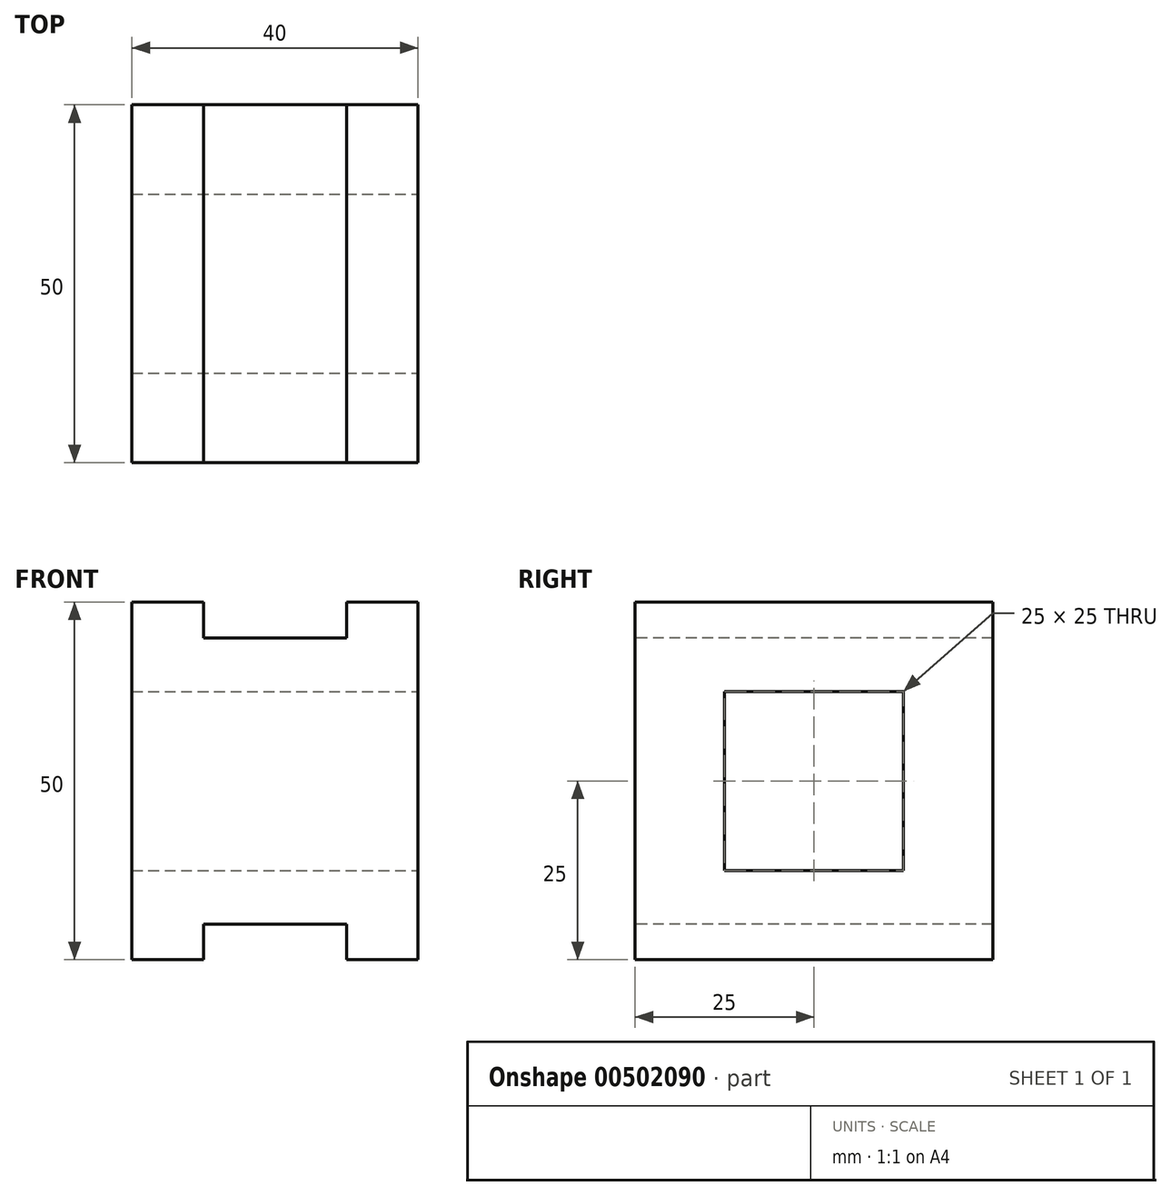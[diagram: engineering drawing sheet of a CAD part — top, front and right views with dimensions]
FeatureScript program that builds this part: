
annotation { "Feature Type Name" : "Feature", "Feature Type Description" : "" }
export const myFeature = defineFeature(function(context is Context, id is Id, definition is map)
    precondition{}
    {
        {
            var Q0;
            Q0=qCreatedBy(makeId("Front.planeOp"),FACE);
            var sketch = newSketch(context, id + "F0", { "sketchPlane" : qUnion([Q0])});
            skLineSegment(sketch, "E0.bottom", {"start": v(0, 0) * mm, "end": v(40, 0) * mm});
            skLineSegment(sketch, "E0.top", {"start": v(0, 50) * mm, "end": v(40, 50) * mm});
            skLineSegment(sketch, "E0.left", {"start": v(0, 0) * mm, "end": v(0, 50) * mm});
            skLineSegment(sketch, "E0.right", {"start": v(40, 0) * mm, "end": v(40, 50) * mm});
            skSolve(sketch);
        }
        {
            var Q0;
            Q0=makeQuery(id+"F0.imprint","IMPRINT",FACE,{"disambiguationData":[TD([[makeQuery(id+"F0.imprint","IMPRINT",EDGE,{"derivedFrom":sQuery(id+"F0.wireOp",EDGE,"E0.bottom")}),1.0]])]});
            extrude(context, id + "F1", {"entities" : qUnion([Q0]), "oppositeDirection" : true, "depth" : 50 * mm, "offsetDistance" : 25 * mm});
        }
        {
            var Q0;
            Q0=makeQuery(id+"F1.opExtrude","SWEPT_FACE",FACE,{"disambiguationData":[OSD([sQuery(id+"F0.wireOp",EDGE,"E0.right")])]});
            var sketch = newSketch(context, id + "F2", { "sketchPlane" : qUnion([Q0])});
            skLineSegment(sketch, "E1.bottom", {"start": v(12.5, 12.5) * mm, "end": v(37.5, 12.5) * mm});
            skLineSegment(sketch, "E1.top", {"start": v(12.5, 37.5) * mm, "end": v(37.5, 37.5) * mm});
            skLineSegment(sketch, "E1.left", {"start": v(12.5, 12.5) * mm, "end": v(12.5, 37.5) * mm});
            skLineSegment(sketch, "E1.right", {"start": v(37.5, 12.5) * mm, "end": v(37.5, 37.5) * mm});
            skSolve(sketch);
        }
        {
            var Q0;
            Q0=makeQuery(id+"F2.imprint","IMPRINT",FACE,{"disambiguationData":[TD([[makeQuery(id+"F2.imprint","IMPRINT",EDGE,{"derivedFrom":sQuery(id+"F2.wireOp",EDGE,"E1.bottom")}),1.0]])]});
            extrude(context, id + "F3", {"entities" : qUnion([Q0]), "oppositeDirection" : true, "depth" : 139.9 * mm, "offsetDistance" : 25 * mm, "hasSecondDirection" : true, "secondDirectionOppositeDirection" : false, "secondDirectionDepth" : 82.6 * mm});
        }
        {
            var Q0;
            Q0=makeQuery(id+"F3.opExtrude","SWEPT_BODY",BODY,{"disambiguationData":[OSD([sQuery(id+"F2.wireOp",EDGE,"E1.bottom"),sQuery(id+"F2.wireOp",EDGE,"E1.top"),sQuery(id+"F2.wireOp",EDGE,"E1.left"),sQuery(id+"F2.wireOp",EDGE,"E1.right")])]});
            var Q1;
            Q1=makeQuery(id+"F1.opExtrude","SWEPT_BODY",BODY,{"disambiguationData":[OSD([sQuery(id+"F0.wireOp",EDGE,"E0.bottom"),sQuery(id+"F0.wireOp",EDGE,"E0.top"),sQuery(id+"F0.wireOp",EDGE,"E0.left"),sQuery(id+"F0.wireOp",EDGE,"E0.right")])]});
            booleanBodies(context, id + "F4", {"operationType" : BooleanOperationType.SUBTRACTION, "tools" : qUnion([Q0]), "targets" : qUnion([Q1])});
        }
        {
            var Q0;
            Q0=makeQuery(id+"F1.opExtrude","SWEPT_FACE",FACE,{"disambiguationData":[OSD([sQuery(id+"F0.wireOp",EDGE,"E0.top")])]});
            var sketch = newSketch(context, id + "F5", { "sketchPlane" : qUnion([Q0])});
            skLineSegment(sketch, "E2.bottom", {"start": v(10, 50) * mm, "end": v(30, 50) * mm});
            skLineSegment(sketch, "E2.top", {"start": v(10, 0) * mm, "end": v(30, 0) * mm});
            skLineSegment(sketch, "E2.left", {"start": v(10, 50) * mm, "end": v(10, 0) * mm});
            skLineSegment(sketch, "E2.right", {"start": v(30, 50) * mm, "end": v(30, 0) * mm});
            skSolve(sketch);
        }
        {
            var Q0;
            Q0=makeQuery(id+"F5.imprint","IMPRINT",FACE,{"disambiguationData":[TD([[makeQuery(id+"F5.imprint","IMPRINT",EDGE,{"derivedFrom":sQuery(id+"F5.wireOp",EDGE,"E2.bottom")}),-1.0]])]});
            extrude(context, id + "F6", {"entities" : qUnion([Q0]), "operationType" : NewBodyOperationType.REMOVE, "oppositeDirection" : true, "depth" : 5 * mm, "offsetDistance" : 25 * mm});
        }
        {
            var Q0;
            Q0=makeQuery(id+"F5.imprint","IMPRINT",FACE,{"disambiguationData":[TD([[makeQuery(id+"F5.imprint","IMPRINT",EDGE,{"derivedFrom":sQuery(id+"F5.wireOp",EDGE,"E2.bottom")}),-1.0]])]});
            extrude(context, id + "F7", {"entities" : qUnion([Q0]), "operationType" : NewBodyOperationType.REMOVE, "oppositeDirection" : true, "depth" : 75.1 * mm, "offsetDistance" : 25 * mm, "hasSecondDirection" : true, "secondDirectionOppositeDirection" : true, "secondDirectionDepth" : 45 * mm});
        }
    });
